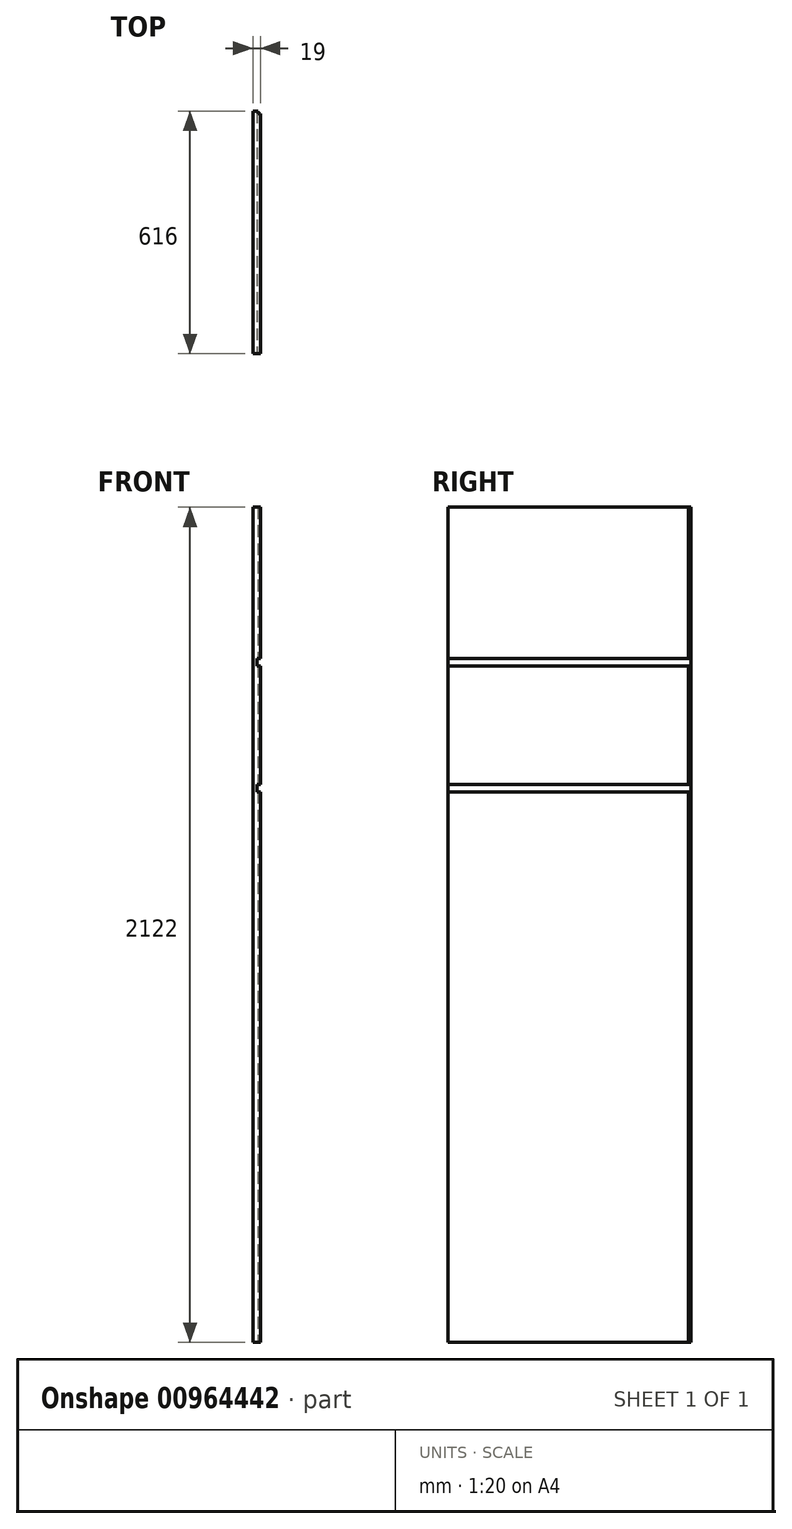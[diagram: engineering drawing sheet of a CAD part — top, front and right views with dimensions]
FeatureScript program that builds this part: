
annotation { "Feature Type Name" : "Feature", "Feature Type Description" : "" }
export const myFeature = defineFeature(function(context is Context, id is Id, definition is map)
    precondition{}
    {
        {
            var Q0;
            Q0=qCreatedBy(makeId("Right.planeOp"),FACE);
            var sketch = newSketch(context, id + "F0", { "sketchPlane" : qUnion([Q0])});
            skLineSegment(sketch, "E0.bottom", {"start": v(0, 0) * mm, "end": v(616, 0) * mm});
            skLineSegment(sketch, "E0.top", {"start": v(0, 2122) * mm, "end": v(616, 2122) * mm});
            skLineSegment(sketch, "E0.left", {"start": v(0, 0) * mm, "end": v(0, 2122) * mm});
            skLineSegment(sketch, "E0.right", {"start": v(616, 0) * mm, "end": v(616, 2122) * mm});
            skSolve(sketch);
        }
        {
            var Q0;
            Q0=makeQuery(id+"F0.imprint","IMPRINT",FACE,{"disambiguationData":[TD([[makeQuery(id+"F0.imprint","IMPRINT",EDGE,{"derivedFrom":sQuery(id+"F0.wireOp",EDGE,"E0.bottom")}),1.0]])]});
            extrude(context, id + "F1", {"entities" : qUnion([Q0]), "depth" : 19 * mm, "offsetDistance" : 25 * mm});
        }
        {
            var Q0;
            Q0=qCreatedBy(makeId("Top.planeOp"),FACE);
            var sketch = newSketch(context, id + "F2", { "sketchPlane" : qUnion([Q0])});
            skLineSegment(sketch, "E1.bottom", {"start": v(19, 616) * mm, "end": v(13, 616) * mm});
            skLineSegment(sketch, "E1.top", {"start": v(19, 610) * mm, "end": v(13, 610) * mm});
            skLineSegment(sketch, "E1.left", {"start": v(19, 616) * mm, "end": v(19, 610) * mm});
            skLineSegment(sketch, "E1.right", {"start": v(13, 616) * mm, "end": v(13, 610) * mm});
            skSolve(sketch);
        }
        {
            var Q0;
            Q0 = qSketchRegion(id + "F2", true);
            extrude(context, id + "F3", {"entities" : qUnion([Q0]), "operationType" : NewBodyOperationType.REMOVE, "endBound" : BoundingType.THROUGH_ALL, "depth" : 25 * mm, "offsetDistance" : 25 * mm});
        }
        {
            var Q0;
            Q0=qCreatedBy(makeId("Front.planeOp"),FACE);
            var sketch = newSketch(context, id + "F4", { "sketchPlane" : qUnion([Q0])});
            skLineSegment(sketch, "E2.bottom", {"start": v(19, 1399) * mm, "end": v(10, 1399) * mm});
            skLineSegment(sketch, "E2.top", {"start": v(19, 1418) * mm, "end": v(10, 1418) * mm});
            skLineSegment(sketch, "E2.left", {"start": v(19, 1399) * mm, "end": v(19, 1418) * mm});
            skLineSegment(sketch, "E2.right", {"start": v(10, 1399) * mm, "end": v(10, 1418) * mm});
            skSolve(sketch);
        }
        {
            var Q0;
            Q0 = qSketchRegion(id + "F4", true);
            extrude(context, id + "F5", {"entities" : qUnion([Q0]), "operationType" : NewBodyOperationType.REMOVE, "endBound" : BoundingType.THROUGH_ALL, "oppositeDirection" : true, "depth" : 25 * mm, "offsetDistance" : 25 * mm});
        }
        {
            var Q0;
            Q0=qCreatedBy(makeId("Front.planeOp"),FACE);
            var sketch = newSketch(context, id + "F6", { "sketchPlane" : qUnion([Q0])});
            skLineSegment(sketch, "E3.bottom", {"start": v(19, 1719) * mm, "end": v(10, 1719) * mm});
            skLineSegment(sketch, "E3.top", {"start": v(19, 1738) * mm, "end": v(10, 1738) * mm});
            skLineSegment(sketch, "E3.left", {"start": v(19, 1719) * mm, "end": v(19, 1738) * mm});
            skLineSegment(sketch, "E3.right", {"start": v(10, 1719) * mm, "end": v(10, 1738) * mm});
            skSolve(sketch);
        }
        {
            var Q0;
            Q0 = qSketchRegion(id + "F6", true);
            extrude(context, id + "F7", {"entities" : qUnion([Q0]), "operationType" : NewBodyOperationType.REMOVE, "endBound" : BoundingType.THROUGH_ALL, "oppositeDirection" : true, "depth" : 25 * mm, "offsetDistance" : 25 * mm});
        }
    });
